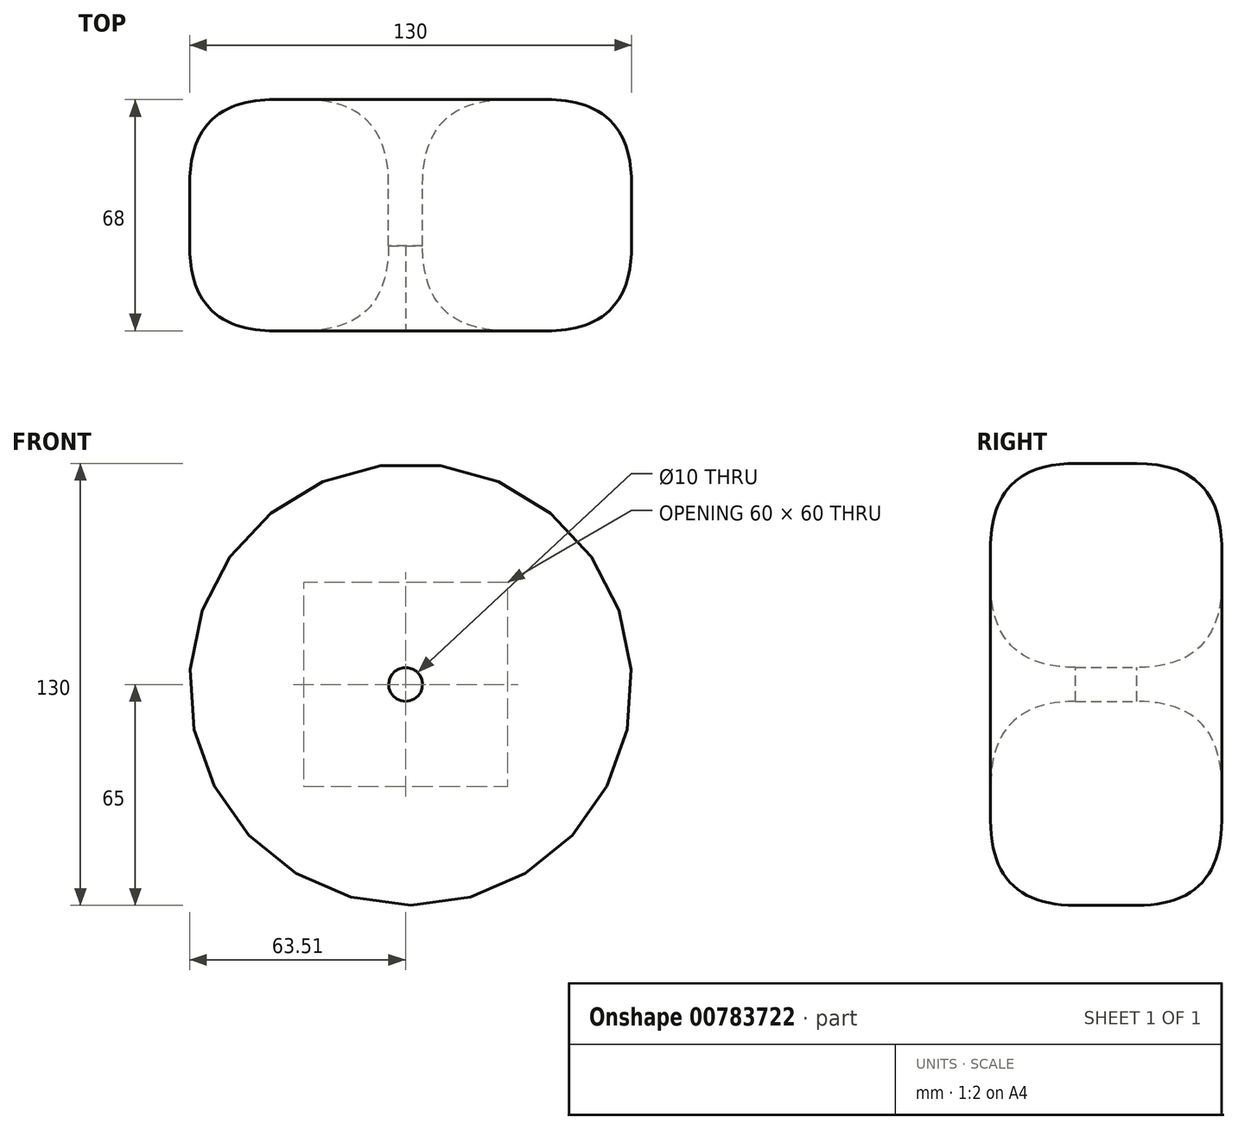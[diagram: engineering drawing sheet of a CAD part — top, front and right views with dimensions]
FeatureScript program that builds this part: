
annotation { "Feature Type Name" : "Feature", "Feature Type Description" : "" }
export const myFeature = defineFeature(function(context is Context, id is Id, definition is map)
    precondition{}
    {
        {
            var Q0;
            Q0=qCreatedBy(makeId("Front.planeOp"),FACE);
            var sketch = newSketch(context, id + "F0", { "sketchPlane" : qUnion([Q0])});
            skCircle(sketch, "E0", {"center": v(1.49, 0) * mm, "radius": 65 * mm});
            skCircle(sketch, "E1", {"center": v(0, 0) * mm, "radius": 5 * mm});
            skSolve(sketch);
        }
        {
            var Q0;
            Q0 = qSketchRegion(id + "F0", true);
            var Q1;
            Q1=makeQuery(id+"F0.imprint","IMPRINT",FACE,{"disambiguationData":[TD([[makeQuery(id+"F0.imprint","IMPRINT",EDGE,{"derivedFrom":sQuery(id+"F0.wireOp",EDGE,"Xh3rmZ6r-mnXF-cQC0-qcFj-POpnVeDtVYFI")}),1.0]])]});
            extrude(context, id + "F1", {"entities" : qUnion([Q0, Q1]), "depth" : 68 * mm, "offsetDistance" : 25 * mm});
        }
        {
            var Q0;
            Q0=makeQuery(id+"F1.opExtrude","CAP_EDGE",EDGE,{"disambiguationData":[OSD([sQuery(id+"F0.wireOp",EDGE,"E0")])],"isStart":false});
            var Q1;
            Q1=makeQuery(id+"F1.opExtrude","CAP_EDGE",EDGE,{"disambiguationData":[OSD([sQuery(id+"F0.wireOp",EDGE,"E0")])],"isStart":true});
            var Q2;
            Q2=makeQuery(id+"F1.opExtrude","CAP_EDGE",EDGE,{"disambiguationData":[OSD([sQuery(id+"F0.wireOp",EDGE,"E1")])],"isStart":false});
            var Q3;
            Q3=makeQuery(id+"F1.opExtrude","CAP_EDGE",EDGE,{"disambiguationData":[OSD([sQuery(id+"F0.wireOp",EDGE,"E1")])],"isStart":true});
            fillet(context, id + "F2", {"entities" : qUnion([Q0, Q1, Q2, Q3]), "radius" : 25 * mm, "tangentPropagation" : true, "rho" : 0.5, "crossSection" : FilletCrossSection.CONIC, "allowEdgeOverflow" : false});
        }
    });
